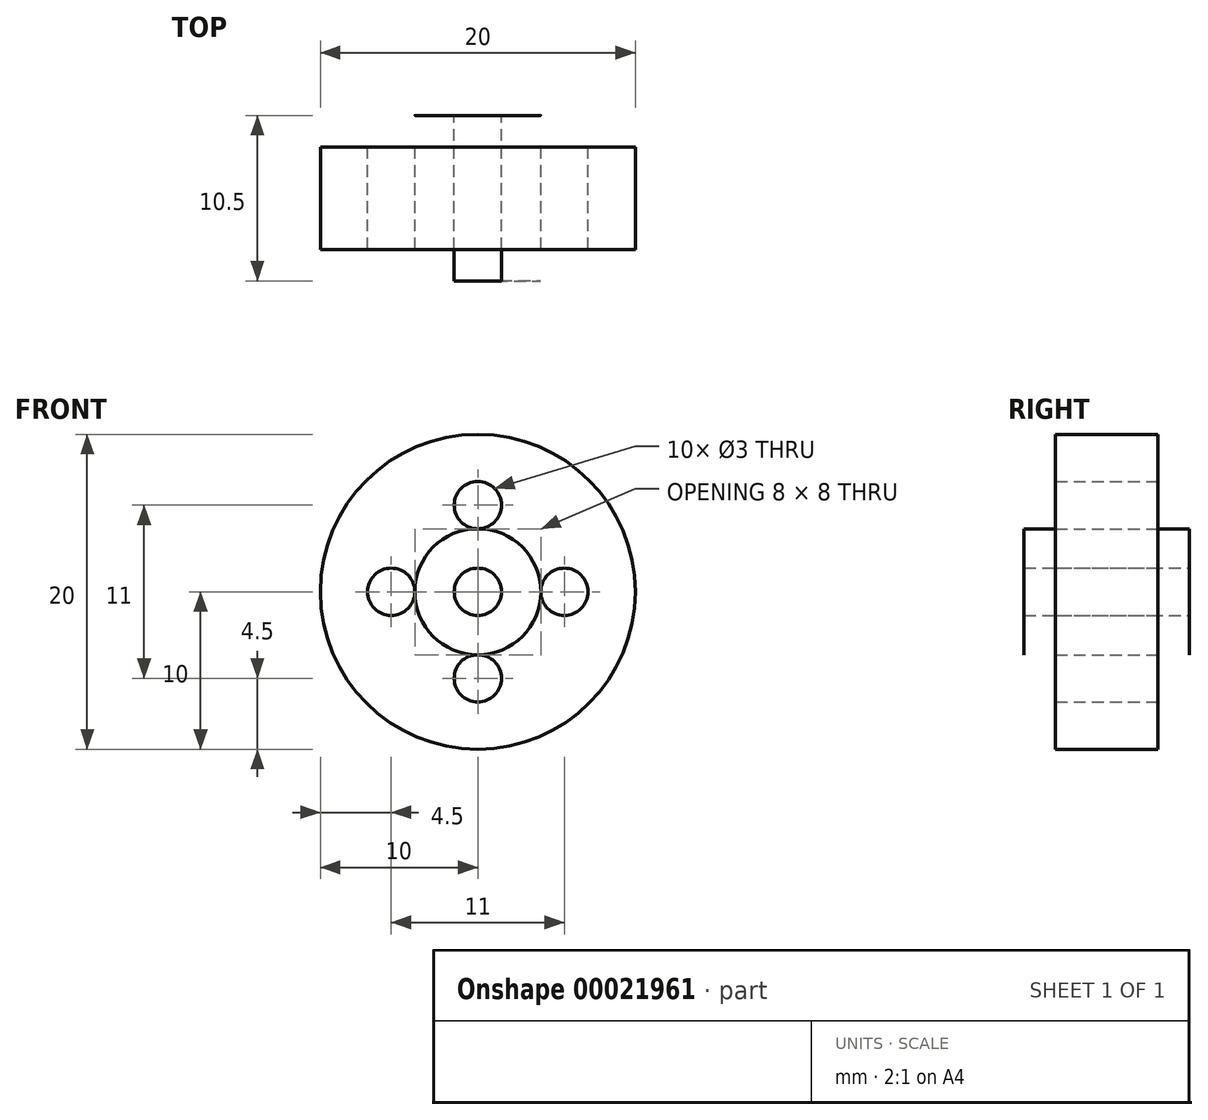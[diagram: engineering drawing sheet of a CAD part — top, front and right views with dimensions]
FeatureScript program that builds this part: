
annotation { "Feature Type Name" : "Feature", "Feature Type Description" : "" }
export const myFeature = defineFeature(function(context is Context, id is Id, definition is map)
    precondition{}
    {
        {
            var Q0;
            Q0=qCreatedBy(makeId("Front.planeOp"),FACE);
            var sketch = newSketch(context, id + "F0", { "sketchPlane" : qUnion([Q0])});
            skCircle(sketch, "E0", {"center": v(0, 0) * mm, "radius": 10 * mm});
            skCircle(sketch, "E1", {"center": v(0, 0) * mm, "radius": 1.5 * mm});
            skCircle(sketch, "E2", {"center": v(0, 0) * mm, "radius": 4 * mm});
            skCircle(sketch, "E3", {"center": v(0, 5.5) * mm, "radius": 1.5 * mm});
            skCircle(sketch, "E4.1.0", {"center": v(-5.5, 0) * mm, "radius": 1.5 * mm});
            skCircle(sketch, "E4.2.0", {"center": v(0, -5.5) * mm, "radius": 1.5 * mm});
            skCircle(sketch, "E4.3.0", {"center": v(5.5, 0) * mm, "radius": 1.5 * mm});
            skSolve(sketch);
        }
        {
            var Q0;
            Q0=qSketchRegion(id+"F0",true);
            var Q1;
            Q1=makeQuery(id+"F0.imprint","IMPRINT",FACE,{"disambiguationData":[TD([[makeQuery(id+"F0.imprint","IMPRINT",EDGE,{"derivedFrom":sQuery(id+"F0.wireOp",EDGE,"acca0e55-db52-494f-9f34-5ed4fc0a81d3")}),-1.0]])]});
            var Q2;
            Q2=makeQuery(id+"F0.imprint","IMPRINT",FACE,{"disambiguationData":[TD([[makeQuery(id+"F0.imprint","IMPRINT",EDGE,{"derivedFrom":sQuery(id+"F0.wireOp",EDGE,"E1")}),-1.0]])]});
            extrude(context, id + "F1", {"entities" : qUnion([Q0, Q1, Q2]), "endBound" : BoundingType.SYMMETRIC, "depth" : 6.5 * mm});
        }
        {
            var Q0;
            Q0=makeQuery(id+"F0.imprint","IMPRINT",FACE,{"disambiguationData":[TD([[makeQuery(id+"F0.imprint","IMPRINT",EDGE,{"derivedFrom":sQuery(id+"F0.wireOp",EDGE,"E1")}),-1.0]])]});
            extrude(context, id + "F2", {"entities" : qUnion([Q0]), "operationType" : NewBodyOperationType.ADD, "endBound" : BoundingType.SYMMETRIC, "depth" : 10.5 * mm});
        }
        {
            var Q0;
            Q0=makeQuery(id+"F0.imprint","IMPRINT",FACE,{"disambiguationData":[TD([[makeQuery(id+"F0.imprint","IMPRINT",EDGE,{"derivedFrom":sQuery(id+"F0.wireOp",EDGE,"E0")}),1.0]])]});
            var Q1;
            {var subQ3=sQuery(id+"F0.wireOp",EDGE,"E3");Q1=makeQuery(id+"F0.imprint","IMPRINT",FACE,{"disambiguationData":[TD([[makeQuery(id+"F0.imprint","IMPRINT",EDGE,{"derivedFrom":subQ3}),-1.0]])]});}
            var Q2;
            Q2=makeQuery(id+"F0.imprint","IMPRINT",FACE,{"disambiguationData":[TD([[makeQuery(id+"F0.imprint","IMPRINT",EDGE,{"derivedFrom":sQuery(id+"F0.wireOp",EDGE,"E1")}),-1.0]])]});
            extrude(context, id + "F3", {"entities" : qUnion([Q0, Q1, Q2]), "endBound" : BoundingType.SYMMETRIC, "depth" : 6.5 * mm});
        }
    });
